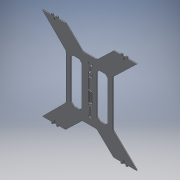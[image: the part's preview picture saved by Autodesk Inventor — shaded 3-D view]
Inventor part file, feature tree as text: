
AUTODESK INVENTOR PART (.ipt)
format: ipt  version: 2019 (Build 230136000, 136)  size: 488,448 bytes
history: native  units: in
note: dims shown in document units (in); Inventor stores cm internally (conversion verified against a paired STEP export)
features: reference x10, other x7, extrude x5, sketch x5, fillet x1, chamfer x1, projected_geometry x1, helix x1
ambient origin geometry x8: Origin, YZ Plane, XZ Plane, XY Plane, X Axis, Y Axis, Z Axis, Center Point
bodies: Solid1 (feature_tree)
feature tree (31):
  extrude  "Extrusion1"  Depth=3.937in
  fillet  "Fillet1"  Radius=3.937in
  extrude  "Extrusion2"  Depth=3.937in
  extrude  "Extrusion3"  Depth=3.937in
  extrude  "Extrusion4"  Depth=2.7559in
  extrude  "Extrusion5"  Depth=0.1575in
  chamfer  "Chamfer1"  Distance=1.0in
  sketch  "Sketch1"  dims[d0=3.937in d1=3.937in d2=3.937in d3=3.937in]
  reference  "Reference1"
  reference  "Reference2"
  sketch  "Sketch2"  dims[d4=4.106in d5=3.937in]
  sketch  "Sketch3"  dims[d6=3.937in d7=3.937in]
  reference  "Reference3"
  reference  "Reference4"
  reference  "Reference5"
  reference  "Reference6"
  sketch  "Sketch4"  dims[d8=2.7559in d9=2.7559in]
  reference  "Reference7"
  reference  "Reference8"
  reference  "Reference9"
  reference  "Reference10"
  sketch  "Sketch5"  dims[d10=0.1575in d11=0.0in d12=0.3937in d13=1.0in d14=0.0in d15=1.0in d16=0.0in d17=1.0in d18=0.0in d19=0.7874in d20=0.7874in d21=1.0in d22=0.0in d23=0.4375in d24=0.125in d25=45.0deg]
  projected_geometry  "Projected Loop1"
  other  "<userpath>\Documents\CAD Files\Helix DLP\Helix DLP Z Stage.iam"
  helix  "Helix DLP Z Stage.iam"  [1 undecoded]
  other  "Z stage_side:1"
  other  "Z stage_side:2"
  other  "Maker_jigsaw_template:2"
  other  "Maker_jigsaw_template:3"
  other  "Maker_jigsaw_template:1"
  other  "Maker_jigsaw_template:4"
note: 1 required parameter value undecoded (feature->parameter linkage not recoverable at this tier; creation-order binding heuristic only, values carry confidence <= 0.55)
